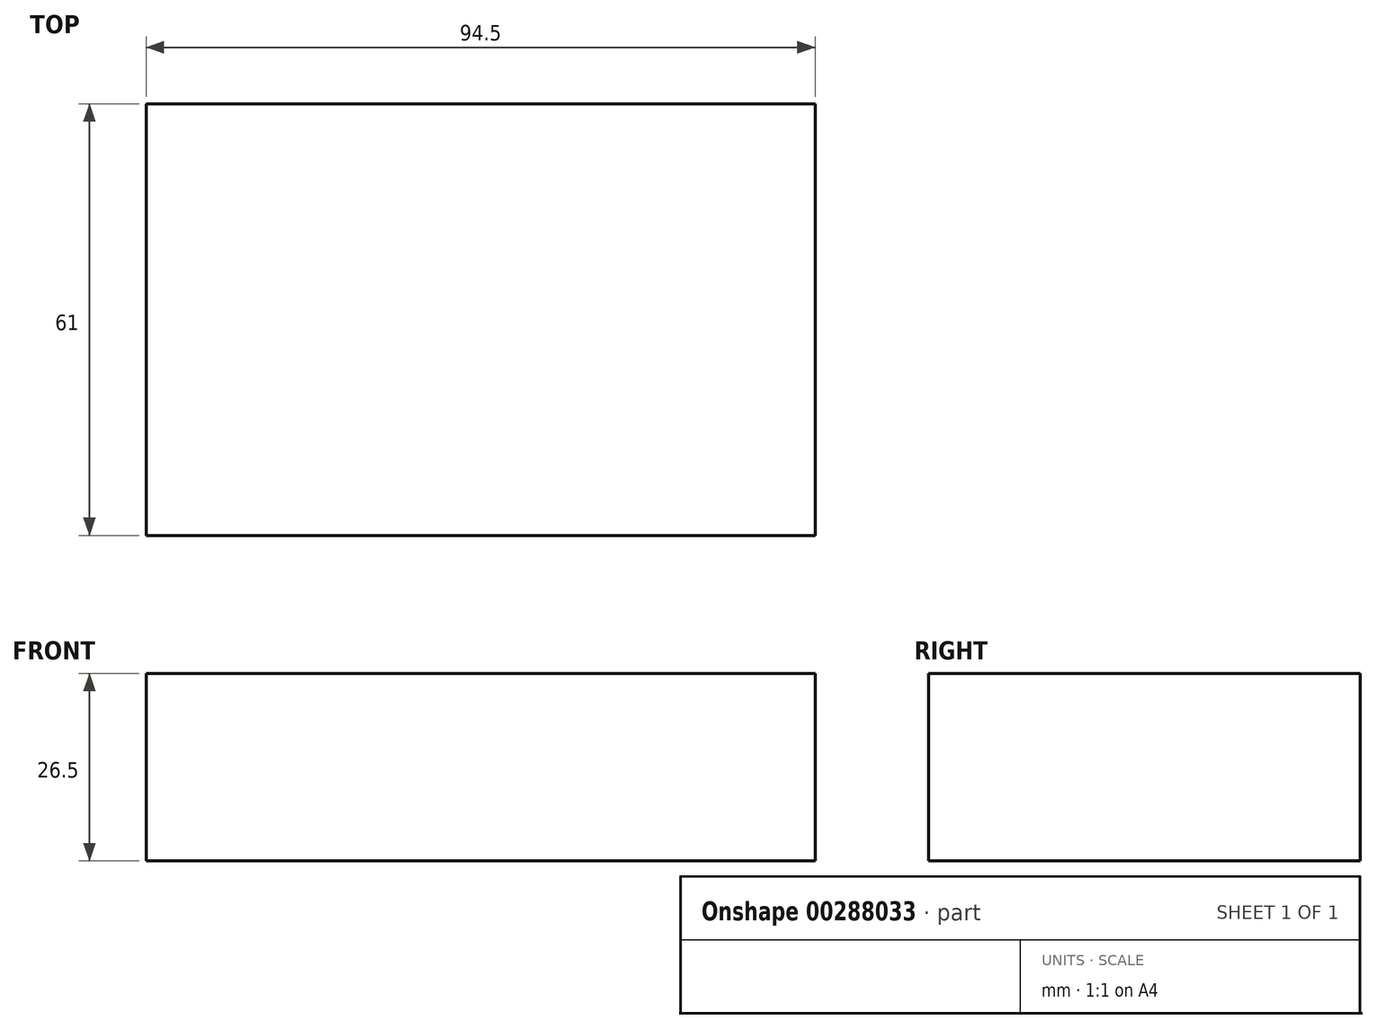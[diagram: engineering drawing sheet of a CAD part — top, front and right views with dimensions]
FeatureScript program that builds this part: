
annotation { "Feature Type Name" : "Feature", "Feature Type Description" : "" }
export const myFeature = defineFeature(function(context is Context, id is Id, definition is map)
    precondition{}
    {
        {
            var Q0;
            Q0=qCreatedBy(makeId("Top.planeOp"),FACE);
            var sketch = newSketch(context, id + "F0", { "sketchPlane" : qUnion([Q0])});
            skLineSegment(sketch, "E0.bottom", {"start": v(47.25, -30.5) * mm, "end": v(-47.25, -30.5) * mm});
            skLineSegment(sketch, "E0.top", {"start": v(47.25, 30.5) * mm, "end": v(-47.25, 30.5) * mm});
            skLineSegment(sketch, "E0.left", {"start": v(47.25, -30.5) * mm, "end": v(47.25, 30.5) * mm});
            skLineSegment(sketch, "E0.right", {"start": v(-47.25, -30.5) * mm, "end": v(-47.25, 30.5) * mm});
            skPoint(sketch, "E0.middle", {"position": v(0, 0) * mm});
            skSolve(sketch);
        }
        {
            var Q0;
            Q0 = qSketchRegion(id + "F0", true);
            extrude(context, id + "F1", {"entities" : qUnion([Q0]), "depth" : 26.5 * mm});
        }
    });
